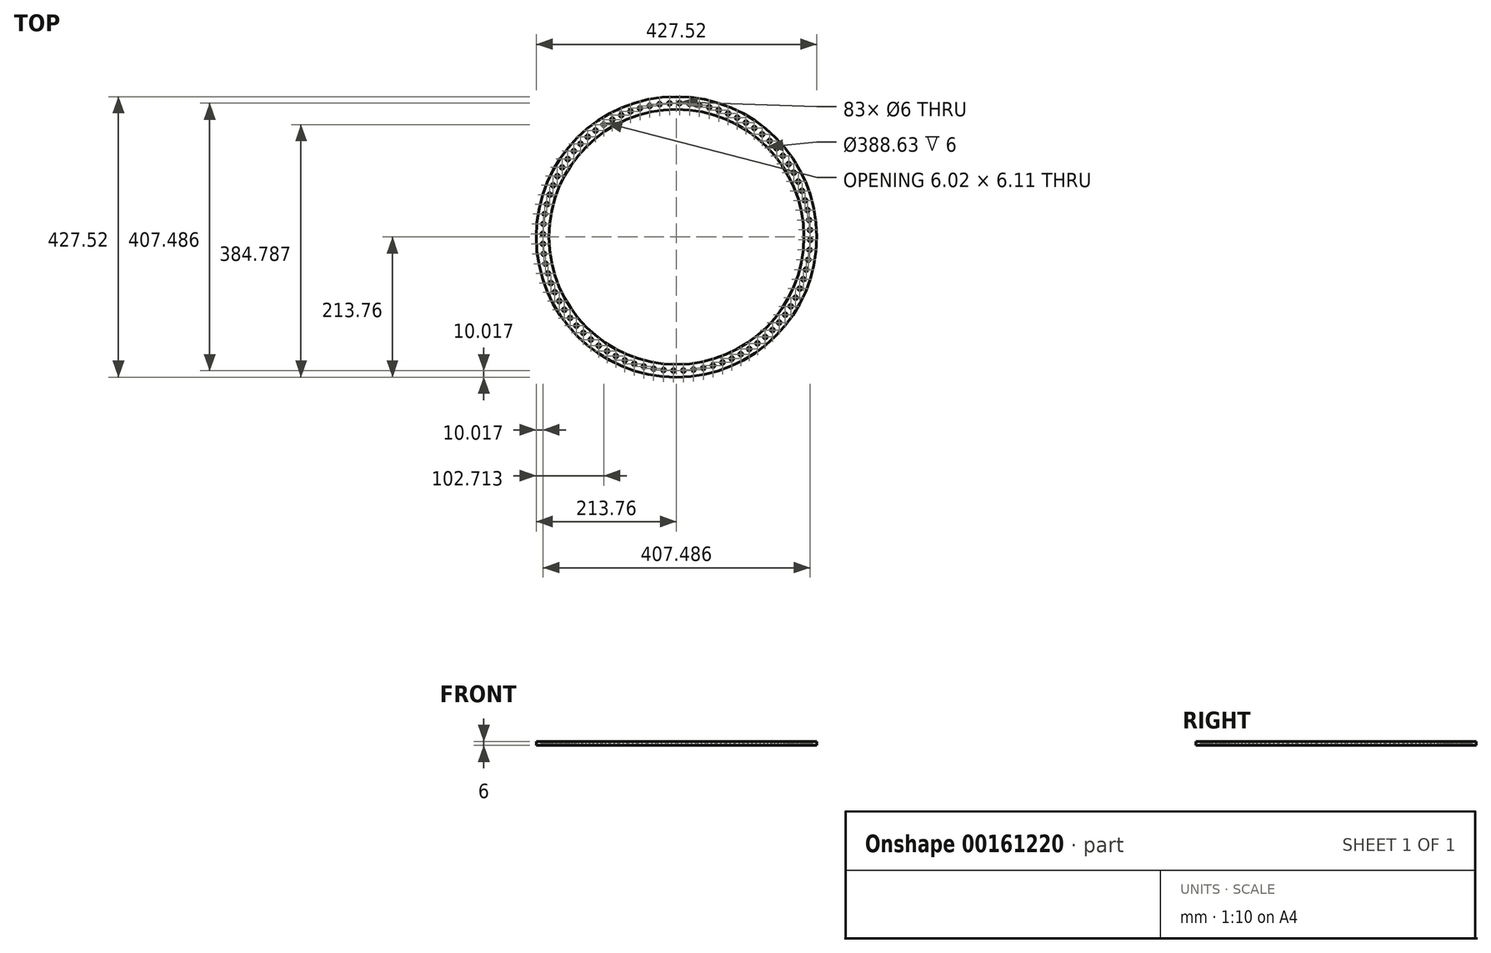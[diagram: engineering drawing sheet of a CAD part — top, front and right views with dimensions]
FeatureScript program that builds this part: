
annotation { "Feature Type Name" : "Feature", "Feature Type Description" : "" }
export const myFeature = defineFeature(function(context is Context, id is Id, definition is map)
    precondition{}
    {
        {
            var Q0;
            Q0=qCreatedBy(makeId("Top.planeOp"),FACE);
            var sketch = newSketch(context, id + "F0", { "sketchPlane" : qUnion([Q0])});
            skCircle(sketch, "E0", {"center": v(0, 0) * mm, "radius": 213.76 * mm});
            skCircle(sketch, "E1", {"center": v(0, 0) * mm, "radius": 194.32 * mm});
            skLineSegment(sketch, "E2", {"start": v(0, 0) * mm, "end": v(-213.76, 0) * mm});
            skLineSegment(sketch, "E3", {"start": v(0, 0) * mm, "end": v(-106.88, 185.12) * mm});
            skPoint(sketch, "E4", {"position": v(-97.16, 168.28) * mm});
            skLineSegment(sketch, "E5", {"start": v(-97.16, 168.28) * mm, "end": v(-101.76, 176.25) * mm});
            skCircle(sketch, "E6", {"center": v(-110.98, 170.93) * mm, "radius": 3 * mm});
            skCircle(sketch, "E7.1.0", {"center": v(-101.46, 154.43) * mm, "radius": 3 * mm});
            skCircle(sketch, "E7.2.0", {"center": v(-101.46, 154.43) * mm, "radius": 3 * mm});
            skCircle(sketch, "E7.3.0", {"center": v(-101.46, 154.43) * mm, "radius": 3 * mm});
            skCircle(sketch, "E7.4.0", {"center": v(-101.46, 154.43) * mm, "radius": 3 * mm});
            skCircle(sketch, "E7.5.0", {"center": v(-101.46, 154.43) * mm, "radius": 3 * mm});
            skCircle(sketch, "E7.7.0", {"center": v(-101.46, 154.43) * mm, "radius": 3 * mm});
            skCircle(sketch, "E7.8.0", {"center": v(-101.46, 154.43) * mm, "radius": 3 * mm});
            skCircle(sketch, "E7.9.0", {"center": v(-101.46, 154.43) * mm, "radius": 3 * mm});
            skCircle(sketch, "E7.10.0", {"center": v(-101.46, 154.43) * mm, "radius": 3 * mm});
            skCircle(sketch, "E7.11.0", {"center": v(-101.46, 154.43) * mm, "radius": 3 * mm});
            skCircle(sketch, "E7.13.0", {"center": v(-101.46, 154.43) * mm, "radius": 3 * mm});
            skCircle(sketch, "E7.14.0", {"center": v(-101.46, 154.43) * mm, "radius": 3 * mm});
            skCircle(sketch, "E7.15.0", {"center": v(-101.46, 154.43) * mm, "radius": 3 * mm});
            skCircle(sketch, "E7.16.0", {"center": v(-101.46, 154.43) * mm, "radius": 3 * mm});
            skCircle(sketch, "E7.17.0", {"center": v(-101.46, 154.43) * mm, "radius": 3 * mm});
            skCircle(sketch, "E7.18.0", {"center": v(-101.46, 154.43) * mm, "radius": 3 * mm});
            skCircle(sketch, "E7.19.0", {"center": v(-101.46, 154.43) * mm, "radius": 3 * mm});
            skCircle(sketch, "E7.20.0", {"center": v(-101.46, 154.43) * mm, "radius": 3 * mm});
            skCircle(sketch, "E7.22.0", {"center": v(-101.46, 154.43) * mm, "radius": 3 * mm});
            skCircle(sketch, "E7.23.0", {"center": v(-101.46, 154.43) * mm, "radius": 3 * mm});
            skCircle(sketch, "E7.24.0", {"center": v(-101.46, 154.43) * mm, "radius": 3 * mm});
            skCircle(sketch, "E7.25.0", {"center": v(-101.46, 154.43) * mm, "radius": 3 * mm});
            skCircle(sketch, "E7.26.0", {"center": v(-101.46, 154.43) * mm, "radius": 3 * mm});
            skCircle(sketch, "E7.27.0", {"center": v(-101.46, 154.43) * mm, "radius": 3 * mm});
            skCircle(sketch, "E7.28.0", {"center": v(-101.46, 154.43) * mm, "radius": 3 * mm});
            skCircle(sketch, "E7.29.0", {"center": v(-101.46, 154.43) * mm, "radius": 3 * mm});
            skPoint(sketch, "E7.center", {"position": v(-9.52, 16.5) * mm});
            skCircle(sketch, "E8.2.0", {"center": v(-142.47, 117.66) * mm, "radius": 3 * mm});
            skCircle(sketch, "E8.3.0", {"center": v(-158.41, 95.11) * mm, "radius": 3 * mm});
            skCircle(sketch, "E8.4.0", {"center": v(-170.82, 70.44) * mm, "radius": 3 * mm});
            skCircle(sketch, "E8.5.0", {"center": v(-179.4, 44.2) * mm, "radius": 3 * mm});
            skCircle(sketch, "E8.6.0", {"center": v(-184, 16.96) * mm, "radius": 3 * mm});
            skCircle(sketch, "E8.7.0", {"center": v(-184.47, -10.65) * mm, "radius": 3 * mm});
            skCircle(sketch, "E8.8.0", {"center": v(-180.82, -38.02) * mm, "radius": 3 * mm});
            skCircle(sketch, "E8.9.0", {"center": v(-173.13, -64.55) * mm, "radius": 3 * mm});
            skCircle(sketch, "E8.10.0", {"center": v(-161.58, -89.63) * mm, "radius": 3 * mm});
            skCircle(sketch, "E8.11.0", {"center": v(-146.41, -112.71) * mm, "radius": 3 * mm});
            skCircle(sketch, "E8.12.0", {"center": v(-127.98, -133.28) * mm, "radius": 3 * mm});
            skCircle(sketch, "E8.13.0", {"center": v(-106.69, -150.86) * mm, "radius": 3 * mm});
            skCircle(sketch, "E8.14.0", {"center": v(-83, -165.08) * mm, "radius": 3 * mm});
            skCircle(sketch, "E8.15.0", {"center": v(-57.48, -175.6) * mm, "radius": 3 * mm});
            skCircle(sketch, "E8.16.0", {"center": v(-30.66, -182.21) * mm, "radius": 3 * mm});
            skCircle(sketch, "E8.17.0", {"center": v(-3.16, -184.75) * mm, "radius": 3 * mm});
            skCircle(sketch, "E8.18.0", {"center": v(24.4, -183.15) * mm, "radius": 3 * mm});
            skCircle(sketch, "E8.19.0", {"center": v(51.43, -177.47) * mm, "radius": 3 * mm});
            skCircle(sketch, "E8.20.0", {"center": v(77.3, -167.82) * mm, "radius": 3 * mm});
            skCircle(sketch, "E8.21.0", {"center": v(101.46, -154.43) * mm, "radius": 3 * mm});
            skCircle(sketch, "E8.22.0", {"center": v(123.34, -137.58) * mm, "radius": 3 * mm});
            skCircle(sketch, "E8.23.0", {"center": v(142.47, -117.66) * mm, "radius": 3 * mm});
            skCircle(sketch, "E8.24.0", {"center": v(158.41, -95.11) * mm, "radius": 3 * mm});
            skCircle(sketch, "E8.25.0", {"center": v(170.82, -70.44) * mm, "radius": 3 * mm});
            skCircle(sketch, "E8.26.0", {"center": v(179.4, -44.2) * mm, "radius": 3 * mm});
            skCircle(sketch, "E8.27.0", {"center": v(184, -16.96) * mm, "radius": 3 * mm});
            skCircle(sketch, "E8.28.0", {"center": v(184.47, 10.65) * mm, "radius": 3 * mm});
            skCircle(sketch, "E8.29.0", {"center": v(180.82, 38.02) * mm, "radius": 3 * mm});
            skCircle(sketch, "E9.1.83.0", {"center": v(-111.11, 171.13) * mm, "radius": 3 * mm});
            skCircle(sketch, "E10.1.30.0", {"center": v(173.13, 64.55) * mm, "radius": 3 * mm});
            skCircle(sketch, "E10.1.31.0", {"center": v(161.58, 89.63) * mm, "radius": 3 * mm});
            skCircle(sketch, "E10.1.32.0", {"center": v(146.41, 112.71) * mm, "radius": 3 * mm});
            skCircle(sketch, "E10.1.33.0", {"center": v(127.98, 133.28) * mm, "radius": 3 * mm});
            skCircle(sketch, "E10.1.34.0", {"center": v(106.69, 150.86) * mm, "radius": 3 * mm});
            skCircle(sketch, "E10.1.35.0", {"center": v(83, 165.08) * mm, "radius": 3 * mm});
            skCircle(sketch, "E10.1.36.0", {"center": v(57.48, 175.6) * mm, "radius": 3 * mm});
            skCircle(sketch, "E10.1.37.0", {"center": v(30.66, 182.21) * mm, "radius": 3 * mm});
            skCircle(sketch, "E10.1.38.0", {"center": v(3.16, 184.75) * mm, "radius": 3 * mm});
            skCircle(sketch, "E10.1.41.0", {"center": v(-77.3, 167.82) * mm, "radius": 3 * mm});
            skCircle(sketch, "E11.1.0", {"center": v(-123.44, 162.15) * mm, "radius": 3 * mm});
            skCircle(sketch, "E11.2.0", {"center": v(-135.22, 152.48) * mm, "radius": 3 * mm});
            skCircle(sketch, "E11.3.0", {"center": v(-146.23, 141.94) * mm, "radius": 3 * mm});
            skCircle(sketch, "E11.4.0", {"center": v(-156.43, 130.62) * mm, "radius": 3 * mm});
            skCircle(sketch, "E11.5.0", {"center": v(-165.76, 118.56) * mm, "radius": 3 * mm});
            skCircle(sketch, "E11.6.0", {"center": v(-174.15, 105.85) * mm, "radius": 3 * mm});
            skCircle(sketch, "E11.7.0", {"center": v(-181.58, 92.53) * mm, "radius": 3 * mm});
            skCircle(sketch, "E11.8.0", {"center": v(-187.98, 78.7) * mm, "radius": 3 * mm});
            skCircle(sketch, "E11.9.0", {"center": v(-193.34, 64.44) * mm, "radius": 3 * mm});
            skCircle(sketch, "E11.10.0", {"center": v(-197.61, 49.81) * mm, "radius": 3 * mm});
            skCircle(sketch, "E11.11.0", {"center": v(-200.78, 34.9) * mm, "radius": 3 * mm});
            skCircle(sketch, "E11.12.0", {"center": v(-202.83, 19.8) * mm, "radius": 3 * mm});
            skCircle(sketch, "E11.13.0", {"center": v(-203.74, 4.59) * mm, "radius": 3 * mm});
            skCircle(sketch, "E11.14.0", {"center": v(-203.52, -10.65) * mm, "radius": 3 * mm});
            skCircle(sketch, "E11.15.0", {"center": v(-202.15, -25.83) * mm, "radius": 3 * mm});
            skCircle(sketch, "E11.16.0", {"center": v(-199.66, -40.86) * mm, "radius": 3 * mm});
            skCircle(sketch, "E11.17.0", {"center": v(-196.04, -55.67) * mm, "radius": 3 * mm});
            skCircle(sketch, "E11.18.0", {"center": v(-191.34, -70.16) * mm, "radius": 3 * mm});
            skCircle(sketch, "E11.19.0", {"center": v(-185.56, -84.27) * mm, "radius": 3 * mm});
            skCircle(sketch, "E11.20.0", {"center": v(-178.74, -97.9) * mm, "radius": 3 * mm});
            skCircle(sketch, "E11.21.0", {"center": v(-170.93, -110.98) * mm, "radius": 3 * mm});
            skCircle(sketch, "E11.22.0", {"center": v(-162.15, -123.44) * mm, "radius": 3 * mm});
            skCircle(sketch, "E11.23.0", {"center": v(-152.48, -135.22) * mm, "radius": 3 * mm});
            skCircle(sketch, "E11.24.0", {"center": v(-141.94, -146.23) * mm, "radius": 3 * mm});
            skCircle(sketch, "E11.25.0", {"center": v(-130.62, -156.43) * mm, "radius": 3 * mm});
            skCircle(sketch, "E11.26.0", {"center": v(-118.56, -165.76) * mm, "radius": 3 * mm});
            skCircle(sketch, "E11.27.0", {"center": v(-105.85, -174.15) * mm, "radius": 3 * mm});
            skCircle(sketch, "E11.28.0", {"center": v(-92.53, -181.58) * mm, "radius": 3 * mm});
            skCircle(sketch, "E11.29.0", {"center": v(-78.7, -187.98) * mm, "radius": 3 * mm});
            skCircle(sketch, "E11.30.0", {"center": v(-64.44, -193.34) * mm, "radius": 3 * mm});
            skCircle(sketch, "E11.31.0", {"center": v(-49.81, -197.61) * mm, "radius": 3 * mm});
            skCircle(sketch, "E11.32.0", {"center": v(-34.9, -200.78) * mm, "radius": 3 * mm});
            skCircle(sketch, "E11.33.0", {"center": v(-19.8, -202.83) * mm, "radius": 3 * mm});
            skCircle(sketch, "E11.34.0", {"center": v(-4.59, -203.74) * mm, "radius": 3 * mm});
            skCircle(sketch, "E11.35.0", {"center": v(10.65, -203.52) * mm, "radius": 3 * mm});
            skCircle(sketch, "E11.36.0", {"center": v(25.83, -202.15) * mm, "radius": 3 * mm});
            skCircle(sketch, "E11.37.0", {"center": v(40.86, -199.66) * mm, "radius": 3 * mm});
            skCircle(sketch, "E11.38.0", {"center": v(55.67, -196.04) * mm, "radius": 3 * mm});
            skCircle(sketch, "E11.39.0", {"center": v(70.16, -191.34) * mm, "radius": 3 * mm});
            skCircle(sketch, "E11.40.0", {"center": v(84.27, -185.56) * mm, "radius": 3 * mm});
            skCircle(sketch, "E11.41.0", {"center": v(97.9, -178.74) * mm, "radius": 3 * mm});
            skCircle(sketch, "E12.1.42.0", {"center": v(110.98, -170.93) * mm, "radius": 3 * mm});
            skCircle(sketch, "E12.1.43.0", {"center": v(123.44, -162.15) * mm, "radius": 3 * mm});
            skCircle(sketch, "E12.1.44.0", {"center": v(135.22, -152.48) * mm, "radius": 3 * mm});
            skCircle(sketch, "E12.1.45.0", {"center": v(146.23, -141.94) * mm, "radius": 3 * mm});
            skCircle(sketch, "E12.1.46.0", {"center": v(156.43, -130.62) * mm, "radius": 3 * mm});
            skCircle(sketch, "E12.1.47.0", {"center": v(165.76, -118.56) * mm, "radius": 3 * mm});
            skCircle(sketch, "E12.1.48.0", {"center": v(174.15, -105.85) * mm, "radius": 3 * mm});
            skCircle(sketch, "E12.1.49.0", {"center": v(181.58, -92.53) * mm, "radius": 3 * mm});
            skCircle(sketch, "E12.1.50.0", {"center": v(187.98, -78.7) * mm, "radius": 3 * mm});
            skCircle(sketch, "E12.1.51.0", {"center": v(193.34, -64.44) * mm, "radius": 3 * mm});
            skCircle(sketch, "E12.1.52.0", {"center": v(197.61, -49.81) * mm, "radius": 3 * mm});
            skCircle(sketch, "E12.1.53.0", {"center": v(200.78, -34.9) * mm, "radius": 3 * mm});
            skCircle(sketch, "E12.1.54.0", {"center": v(202.83, -19.8) * mm, "radius": 3 * mm});
            skCircle(sketch, "E12.1.55.0", {"center": v(203.74, -4.59) * mm, "radius": 3 * mm});
            skCircle(sketch, "E12.1.56.0", {"center": v(203.52, 10.65) * mm, "radius": 3 * mm});
            skCircle(sketch, "E12.1.57.0", {"center": v(202.15, 25.83) * mm, "radius": 3 * mm});
            skCircle(sketch, "E12.1.58.0", {"center": v(199.66, 40.86) * mm, "radius": 3 * mm});
            skCircle(sketch, "E12.1.59.0", {"center": v(196.04, 55.67) * mm, "radius": 3 * mm});
            skCircle(sketch, "E12.1.60.0", {"center": v(191.34, 70.16) * mm, "radius": 3 * mm});
            skCircle(sketch, "E12.1.61.0", {"center": v(185.56, 84.27) * mm, "radius": 3 * mm});
            skCircle(sketch, "E12.1.62.0", {"center": v(178.74, 97.9) * mm, "radius": 3 * mm});
            skCircle(sketch, "E12.1.63.0", {"center": v(170.93, 110.98) * mm, "radius": 3 * mm});
            skCircle(sketch, "E12.1.64.0", {"center": v(162.15, 123.44) * mm, "radius": 3 * mm});
            skCircle(sketch, "E12.1.65.0", {"center": v(152.48, 135.22) * mm, "radius": 3 * mm});
            skCircle(sketch, "E12.1.66.0", {"center": v(141.94, 146.23) * mm, "radius": 3 * mm});
            skCircle(sketch, "E12.1.67.0", {"center": v(130.62, 156.43) * mm, "radius": 3 * mm});
            skCircle(sketch, "E12.1.68.0", {"center": v(118.56, 165.76) * mm, "radius": 3 * mm});
            skCircle(sketch, "E12.1.69.0", {"center": v(105.85, 174.15) * mm, "radius": 3 * mm});
            skCircle(sketch, "E12.1.70.0", {"center": v(92.53, 181.58) * mm, "radius": 3 * mm});
            skCircle(sketch, "E12.1.71.0", {"center": v(78.7, 187.98) * mm, "radius": 3 * mm});
            skCircle(sketch, "E12.1.72.0", {"center": v(64.44, 193.34) * mm, "radius": 3 * mm});
            skCircle(sketch, "E12.1.73.0", {"center": v(49.81, 197.61) * mm, "radius": 3 * mm});
            skCircle(sketch, "E12.1.74.0", {"center": v(34.9, 200.78) * mm, "radius": 3 * mm});
            skCircle(sketch, "E12.1.75.0", {"center": v(19.8, 202.83) * mm, "radius": 3 * mm});
            skCircle(sketch, "E12.1.76.0", {"center": v(4.59, 203.74) * mm, "radius": 3 * mm});
            skCircle(sketch, "E12.1.77.0", {"center": v(-10.65, 203.52) * mm, "radius": 3 * mm});
            skCircle(sketch, "E12.1.78.0", {"center": v(-25.83, 202.15) * mm, "radius": 3 * mm});
            skCircle(sketch, "E12.1.79.0", {"center": v(-40.86, 199.66) * mm, "radius": 3 * mm});
            skCircle(sketch, "E12.1.80.0", {"center": v(-55.67, 196.04) * mm, "radius": 3 * mm});
            skCircle(sketch, "E12.1.81.0", {"center": v(-70.16, 191.34) * mm, "radius": 3 * mm});
            skCircle(sketch, "E12.1.82.0", {"center": v(-84.27, 185.56) * mm, "radius": 3 * mm});
            skCircle(sketch, "E12.1.83.0", {"center": v(-97.9, 178.74) * mm, "radius": 3 * mm});
            skSolve(sketch);
        }
        {
            var Q0;
            {var subQ0=sQuery(id+"F0.wireOp",EDGE,"E2");var subQ1=sQuery(id+"F0.wireOp",EDGE,"E0");var subQ2=makeQuery(id+"F0.imprint","INTERSECT",VERTEX,{"derivedFrom":[subQ1,subQ0]});Q0=makeQuery(id+"F0.imprint","IMPRINT",FACE,{"disambiguationData":[TD([[makeQuery(id+"F0.imprint","IMPRINT",EDGE,{"disambiguationData":[TD([[subQ2,-1.0]])],"derivedFrom":subQ1}),1.0]])]});}
            var Q1;
            {var subQ0=sQuery(id+"F0.wireOp",EDGE,"E2");var subQ1=sQuery(id+"F0.wireOp",EDGE,"E0");var subQ2=makeQuery(id+"F0.imprint","INTERSECT",VERTEX,{"derivedFrom":[subQ1,subQ0]});Q1=makeQuery(id+"F0.imprint","IMPRINT",FACE,{"disambiguationData":[TD([[makeQuery(id+"F0.imprint","IMPRINT",EDGE,{"disambiguationData":[TD([[subQ2,1.0]])],"derivedFrom":subQ1}),1.0]])]});}
            extrude(context, id + "F1", {"entities" : qUnion([Q0, Q1]), "depth" : 6 * mm});
        }
    });
